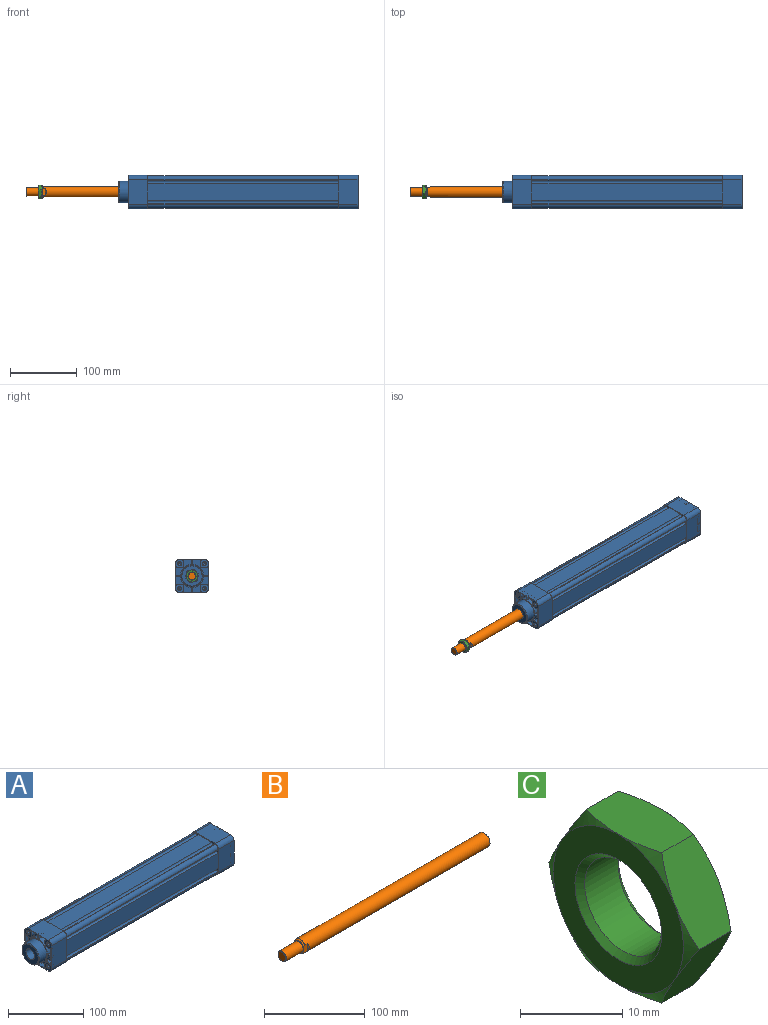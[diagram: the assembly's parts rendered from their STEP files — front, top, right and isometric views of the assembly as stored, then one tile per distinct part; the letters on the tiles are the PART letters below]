
ASSEMBLY  parts=3 mates=2
PART A: 303 faces, bbox 358x50x50 mm
  f0: plane 30.08x30.08mm, normal (-1,0,0), area 509.6mm2, adj f46,f302
  f1: plane 37x29mm, normal (0,1,0), area 866.6mm2, adj f3,f37,f43,f44,f276,f293
  f2: plane 37x29mm, normal (0,1,0), area 866.6mm2, adj f4,f29,f35,f36,f273,f281
  f3: plane 50x50mm, normal (1,0,0), area 1558.8mm2, adj f1,f37,f38,f39,f40,f41,f42,f43
  f4: plane 50x50mm, normal (-1,0,0), area 754.5mm2, adj f2,f29,f30,f31,f32,f33,f34,f35
  f5: cylinder r=2.5mm len=285mm, axis (-1,0,0), area 2238.4mm2, adj f6,f28,f36,f44
  f6: plane 285x1mm, normal (0,1,0), area 285mm2, adj f5,f7,f36,f44
  f7: cylinder r=5.5mm len=285mm, axis (-1,0,0), area 2462.2mm2, adj f6,f8,f36,f44
  f8: plane 285x1mm, normal (0,0,1), area 285mm2, adj f7,f9,f36,f44
  f9: cylinder r=2.5mm len=285mm, axis (-1,0,0), area 2238.4mm2, adj f8,f10,f36,f44
  f10: plane 285x25mm, normal (0,0,1), area 7125mm2, adj f9,f11,f36,f44
  f11: cylinder r=2.5mm len=285mm, axis (-1,0,0), area 2238.4mm2, adj f10,f12,f36,f44
  f12: plane 285x1mm, normal (0,0,1), area 285mm2, adj f11,f13,f36,f44
  f13: cylinder r=5.5mm len=285mm, axis (-1,0,0), area 2462.2mm2, adj f12,f14,f36,f44
  f14: plane 285x1mm, normal (0,-1,0), area 285mm2, adj f13,f15,f36,f44
  f15: cylinder r=2.5mm len=285mm, axis (-1,0,0), area 2238.4mm2, adj f14,f16,f36,f44
  f16: plane 285x25mm, normal (0,-1,0), area 7125mm2, adj f15,f17,f36,f44
  f17: cylinder r=2.5mm len=285mm, axis (-1,0,0), area 2238.4mm2, adj f16,f18,f36,f44
  f18: plane 285x1mm, normal (0,-1,0), area 285mm2, adj f17,f19,f36,f44
  f19: cylinder r=5.5mm len=285mm, axis (-1,0,0), area 2462.2mm2, adj f18,f20,f36,f44
  f20: plane 285x1mm, normal (0,0,-1), area 285mm2, adj f19,f21,f36,f44
  f21: cylinder r=2.5mm len=285mm, axis (-1,0,0), area 2238.4mm2, adj f20,f22,f36,f44
  f22: plane 285x25mm, normal (0,0,-1), area 7125mm2, adj f21,f23,f36,f44
  f23: cylinder r=2.5mm len=285mm, axis (-1,0,0), area 2238.4mm2, adj f22,f24,f36,f44
  f24: plane 285x1mm, normal (0,0,-1), area 285mm2, adj f23,f25,f36,f44
  f25: cylinder r=5.5mm len=285mm, axis (-1,0,0), area 2462.2mm2, adj f24,f26,f36,f44
  f26: plane 285x1mm, normal (0,1,0), area 285mm2, adj f25,f27,f36,f44
  f27: cylinder r=2.5mm len=285mm, axis (-1,0,0), area 2238.4mm2, adj f26,f28,f36,f44
  f28: plane 285x25mm, normal (0,1,0), area 7125mm2, adj f5,f27,f36,f44
  f29: cylinder r=6.5mm len=29mm, axis (-1,0,0), area 296.1mm2, adj f2,f4,f30,f36
  f30: plane 37x29mm, normal (0,0,1), area 1073mm2, adj f4,f29,f31,f36
  f31: cylinder r=6.5mm len=29mm, axis (-1,0,0), area 296.1mm2, adj f4,f30,f32,f36
  f32: plane 37x29mm, normal (0,-1,0), area 1073mm2, adj f4,f31,f33,f36
  f33: cylinder r=6.5mm len=29mm, axis (-1,0,0), area 296.1mm2, adj f4,f32,f34,f36
  f34: plane 37x29mm, normal (0,0,-1), area 1073mm2, adj f4,f33,f35,f36
  f35: cylinder r=6.5mm len=29mm, axis (-1,0,0), area 296.1mm2, adj f2,f4,f34,f36
  f36: plane 50x50mm, normal (1,0,0), area 264.2mm2, adj f2,f5,f6,f7,f8,f9,f10,f11
  f37: cylinder r=6.5mm len=29mm, axis (1,0,0), area 296.1mm2, adj f1,f3,f38,f44
  f38: plane 37x29mm, normal (0,0,-1), area 1073mm2, adj f3,f37,f39,f44
  f39: cylinder r=6.5mm len=29mm, axis (1,0,0), area 296.1mm2, adj f3,f38,f40,f44
  f40: plane 37x29mm, normal (0,-1,0), area 1073mm2, adj f3,f39,f41,f44
  f41: cylinder r=6.5mm len=29mm, axis (1,0,0), area 296.1mm2, adj f3,f40,f42,f44
  f42: plane 37x29mm, normal (0,0,1), area 1073mm2, adj f3,f41,f43,f44
  f43: cylinder r=6.5mm len=29mm, axis (1,0,0), area 296.1mm2, adj f1,f3,f42,f44
  f44: plane 50x50mm, normal (-1,0,0), area 264.2mm2, adj f1,f5,f6,f7,f8,f9,f10,f11
  f45: cylinder r=16mm len=32mm, axis (1,0,0), area 1411.5mm2, adj f4,f46
  f46: torus R=15.04mm, axis (1,0,0), area 148.3mm2, adj f0,f45
  f47: cylinder r=0.54mm len=6.42mm, axis (-1,0,0), area 5.4mm2, adj f4,f48,f56,f57
  f48: plane 12.46x6.42mm, normal (0,-1,0), area 80mm2, adj f4,f47,f49,f57
  f49: cylinder r=0.54mm len=6.42mm, axis (-1,0,0), area 8.2mm2, adj f4,f48,f50,f57
  f50: cylinder r=6.5mm len=8.45mm, axis (-1,0,0), area 59.2mm2, adj f4,f49,f51,f57
  f51: cylinder r=0.54mm len=6.42mm, axis (-1,0,0), area 4.9mm2, adj f4,f50,f52,f57
  f52: plane 6.42x0.89mm, normal (0,0.71,-0.71), area 8.1mm2, adj f4,f51,f53,f57
  f53: cylinder r=0.36mm len=6.42mm, axis (-1,0,0), area 3.5mm2, adj f4,f52,f54,f57
  f54: cylinder r=17.6mm len=10.99mm, axis (-1,0,0), area 77.9mm2, adj f4,f53,f55,f57
  f55: cylinder r=0.36mm len=6.42mm, axis (-1,0,0), area 3.5mm2, adj f4,f54,f56,f57
  f56: plane 6.42x5.52mm, normal (0,0,1), area 35.5mm2, adj f4,f47,f55,f57
  f57: plane 13.54x11.07mm, normal (-1,0,0), area 99mm2, adj f47,f48,f49,f50,f51,f52,f53,f54
  f58: cylinder r=0.54mm len=6.42mm, axis (-1,0,0), area 5.4mm2, adj f4,f59,f67,f68
  f59: plane 12.46x6.42mm, normal (0,0,-1), area 80mm2, adj f4,f58,f60,f68
  f60: cylinder r=0.54mm len=6.42mm, axis (-1,0,0), area 8.2mm2, adj f4,f59,f61,f68
  f61: cylinder r=6.5mm len=8.45mm, axis (-1,0,0), area 59.2mm2, adj f4,f60,f62,f68
  f62: cylinder r=0.54mm len=6.42mm, axis (-1,0,0), area 4.9mm2, adj f4,f61,f63,f68
  f63: plane 6.42x0.89mm, normal (0,0.71,0.71), area 8.1mm2, adj f4,f62,f64,f68
  f64: cylinder r=0.36mm len=6.42mm, axis (-1,0,0), area 3.5mm2, adj f4,f63,f65,f68
  f65: cylinder r=17.6mm len=10.99mm, axis (-1,0,0), area 77.9mm2, adj f4,f64,f66,f68
  f66: cylinder r=0.36mm len=6.42mm, axis (-1,0,0), area 3.5mm2, adj f4,f65,f67,f68
  f67: plane 6.42x5.52mm, normal (0,-1,0), area 35.5mm2, adj f4,f58,f66,f68
  f68: plane 13.54x11.07mm, normal (-1,0,0), area 99mm2, adj f58,f59,f60,f61,f62,f63,f64,f65
  f69: cylinder r=0.54mm len=6.42mm, axis (-1,0,0), area 5.4mm2, adj f4,f70,f78,f79
  f70: plane 12.46x6.42mm, normal (0,1,0), area 80mm2, adj f4,f69,f71,f79
  f71: cylinder r=0.54mm len=6.42mm, axis (-1,0,0), area 8.2mm2, adj f4,f70,f72,f79
  f72: cylinder r=6.5mm len=8.45mm, axis (-1,0,0), area 59.2mm2, adj f4,f71,f73,f79
  f73: cylinder r=0.54mm len=6.42mm, axis (-1,0,0), area 4.9mm2, adj f4,f72,f74,f79
  f74: plane 6.42x0.89mm, normal (0,-0.71,0.71), area 8.1mm2, adj f4,f73,f75,f79
  f75: cylinder r=0.36mm len=6.42mm, axis (-1,0,0), area 3.5mm2, adj f4,f74,f76,f79
  f76: cylinder r=17.6mm len=10.99mm, axis (-1,0,0), area 77.9mm2, adj f4,f75,f77,f79
  f77: cylinder r=0.36mm len=6.42mm, axis (-1,0,0), area 3.5mm2, adj f4,f76,f78,f79
  f78: plane 6.42x5.52mm, normal (0,0,-1), area 35.5mm2, adj f4,f69,f77,f79
  f79: plane 13.54x11.07mm, normal (-1,0,0), area 99mm2, adj f69,f70,f71,f72,f73,f74,f75,f76
  f80: cylinder r=0.54mm len=6.42mm, axis (-1,0,0), area 5.4mm2, adj f4,f81,f89,f90
  f81: plane 12.46x6.42mm, normal (0,0,1), area 80mm2, adj f4,f80,f82,f90
  f82: cylinder r=0.54mm len=6.42mm, axis (-1,0,0), area 8.2mm2, adj f4,f81,f83,f90
  f83: cylinder r=6.5mm len=8.45mm, axis (-1,0,0), area 59.2mm2, adj f4,f82,f84,f90
  f84: cylinder r=0.54mm len=6.42mm, axis (-1,0,0), area 4.9mm2, adj f4,f83,f85,f90
  f85: plane 6.42x0.89mm, normal (0,-0.71,-0.71), area 8.1mm2, adj f4,f84,f86,f90
  f86: cylinder r=0.36mm len=6.42mm, axis (-1,0,0), area 3.5mm2, adj f4,f85,f87,f90
  f87: cylinder r=17.6mm len=10.99mm, axis (-1,0,0), area 77.9mm2, adj f4,f86,f88,f90
  f88: cylinder r=0.36mm len=6.42mm, axis (-1,0,0), area 3.5mm2, adj f4,f87,f89,f90
  f89: plane 6.42x5.52mm, normal (0,1,0), area 35.5mm2, adj f4,f80,f88,f90
  f90: plane 13.54x11.07mm, normal (-1,0,0), area 99mm2, adj f80,f81,f82,f83,f84,f85,f86,f87
  f91: cylinder r=0.54mm len=6.42mm, axis (1,0,0), area 5.4mm2, adj f4,f92,f100,f101
  f92: plane 12.46x6.42mm, normal (0,-1,0), area 80mm2, adj f4,f91,f93,f101
  f93: cylinder r=0.54mm len=6.42mm, axis (1,0,0), area 8.2mm2, adj f4,f92,f94,f101
  f94: cylinder r=6.5mm len=8.45mm, axis (1,0,0), area 59.2mm2, adj f4,f93,f95,f101
  f95: cylinder r=0.54mm len=6.42mm, axis (1,0,0), area 4.9mm2, adj f4,f94,f96,f101
  f96: plane 6.42x0.89mm, normal (0,0.71,0.71), area 8.1mm2, adj f4,f95,f97,f101
  f97: cylinder r=0.36mm len=6.42mm, axis (1,0,0), area 3.5mm2, adj f4,f96,f98,f101
  f98: cylinder r=17.6mm len=10.99mm, axis (1,0,0), area 77.9mm2, adj f4,f97,f99,f101
  f99: cylinder r=0.36mm len=6.42mm, axis (1,0,0), area 3.5mm2, adj f4,f98,f100,f101
  f100: plane 6.42x5.52mm, normal (0,0,-1), area 35.5mm2, adj f4,f91,f99,f101
  f101: plane 13.54x11.07mm, normal (-1,0,0), area 99mm2, adj f91,f92,f93,f94,f95,f96,f97,f98
  f102: cylinder r=0.54mm len=6.42mm, axis (1,0,0), area 5.4mm2, adj f4,f103,f111,f112
  f103: plane 12.46x6.42mm, normal (0,0,-1), area 80mm2, adj f4,f102,f104,f112
  f104: cylinder r=0.54mm len=6.42mm, axis (1,0,0), area 8.2mm2, adj f4,f103,f105,f112
  f105: cylinder r=6.5mm len=8.45mm, axis (1,0,0), area 59.2mm2, adj f4,f104,f106,f112
  f106: cylinder r=0.54mm len=6.42mm, axis (1,0,0), area 4.9mm2, adj f4,f105,f107,f112
  f107: plane 6.42x0.89mm, normal (0,-0.71,0.71), area 8.1mm2, adj f4,f106,f108,f112
  f108: cylinder r=0.36mm len=6.42mm, axis (1,0,0), area 3.5mm2, adj f4,f107,f109,f112
  f109: cylinder r=17.6mm len=10.99mm, axis (1,0,0), area 77.9mm2, adj f4,f108,f110,f112
  f110: cylinder r=0.36mm len=6.42mm, axis (1,0,0), area 3.5mm2, adj f4,f109,f111,f112
  f111: plane 6.42x5.52mm, normal (0,1,0), area 35.5mm2, adj f4,f102,f110,f112
  f112: plane 13.54x11.07mm, normal (-1,0,0), area 99mm2, adj f102,f103,f104,f105,f106,f107,f108,f109
  f113: cylinder r=0.54mm len=6.42mm, axis (1,0,0), area 5.4mm2, adj f4,f114,f122,f123
  f114: plane 12.46x6.42mm, normal (0,1,0), area 80mm2, adj f4,f113,f115,f123
  f115: cylinder r=0.54mm len=6.42mm, axis (1,0,0), area 8.2mm2, adj f4,f114,f116,f123
  f116: cylinder r=6.5mm len=8.45mm, axis (1,0,0), area 59.2mm2, adj f4,f115,f117,f123
  f117: cylinder r=0.54mm len=6.42mm, axis (1,0,0), area 4.9mm2, adj f4,f116,f118,f123
  f118: plane 6.42x0.89mm, normal (0,-0.71,-0.71), area 8.1mm2, adj f4,f117,f119,f123
  f119: cylinder r=0.36mm len=6.42mm, axis (1,0,0), area 3.5mm2, adj f4,f118,f120,f123
  f120: cylinder r=17.6mm len=10.99mm, axis (1,0,0), area 77.9mm2, adj f4,f119,f121,f123
  f121: cylinder r=0.36mm len=6.42mm, axis (1,0,0), area 3.5mm2, adj f4,f120,f122,f123
  f122: plane 6.42x5.52mm, normal (0,0,1), area 35.5mm2, adj f4,f113,f121,f123
  f123: plane 13.54x11.07mm, normal (-1,0,0), area 99mm2, adj f113,f114,f115,f116,f117,f118,f119,f120
  f124: cylinder r=0.54mm len=6.42mm, axis (1,0,0), area 5.4mm2, adj f4,f125,f133,f134
  f125: plane 12.46x6.42mm, normal (0,0,1), area 80mm2, adj f4,f124,f126,f134
  f126: cylinder r=0.54mm len=6.42mm, axis (1,0,0), area 8.2mm2, adj f4,f125,f127,f134
  f127: cylinder r=6.5mm len=8.45mm, axis (1,0,0), area 59.2mm2, adj f4,f126,f128,f134
  f128: cylinder r=0.54mm len=6.42mm, axis (1,0,0), area 4.9mm2, adj f4,f127,f129,f134
  f129: plane 6.42x0.89mm, normal (0,0.71,-0.71), area 8.1mm2, adj f4,f128,f130,f134
  f130: cylinder r=0.36mm len=6.42mm, axis (1,0,0), area 3.5mm2, adj f4,f129,f131,f134
  f131: cylinder r=17.6mm len=10.99mm, axis (1,0,0), area 77.9mm2, adj f4,f130,f132,f134
  f132: cylinder r=0.36mm len=6.42mm, axis (1,0,0), area 3.5mm2, adj f4,f131,f133,f134
  f133: plane 6.42x5.52mm, normal (0,-1,0), area 35.5mm2, adj f4,f124,f132,f134
  f134: plane 13.54x11.07mm, normal (-1,0,0), area 99mm2, adj f124,f125,f126,f127,f128,f129,f130,f131
  f135: cylinder r=0.54mm len=6.42mm, axis (1,0,0), area 5.4mm2, adj f3,f136,f144,f145
  f136: plane 12.46x6.42mm, normal (0,-1,0), area 80mm2, adj f3,f135,f137,f145
  f137: cylinder r=0.54mm len=6.42mm, axis (1,0,0), area 8.2mm2, adj f3,f136,f138,f145
  f138: cylinder r=6.5mm len=8.45mm, axis (1,0,0), area 59.2mm2, adj f3,f137,f139,f145
  f139: cylinder r=0.54mm len=6.42mm, axis (1,0,0), area 4.9mm2, adj f3,f138,f140,f145
  f140: plane 6.42x0.89mm, normal (0,0.71,0.71), area 8.1mm2, adj f3,f139,f141,f145
  f141: cylinder r=0.36mm len=6.42mm, axis (1,0,0), area 3.5mm2, adj f3,f140,f142,f145
  f142: cylinder r=17.6mm len=10.99mm, axis (1,0,0), area 77.9mm2, adj f3,f141,f143,f145
  f143: cylinder r=0.36mm len=6.42mm, axis (1,0,0), area 3.5mm2, adj f3,f142,f144,f145
  f144: plane 6.42x5.52mm, normal (0,0,-1), area 35.5mm2, adj f3,f135,f143,f145
  f145: plane 13.54x11.07mm, normal (1,0,0), area 99mm2, adj f135,f136,f137,f138,f139,f140,f141,f142
  f146: cylinder r=0.54mm len=6.42mm, axis (1,0,0), area 5.4mm2, adj f3,f147,f155,f156
  f147: plane 12.46x6.42mm, normal (0,0,-1), area 80mm2, adj f3,f146,f148,f156
  f148: cylinder r=0.54mm len=6.42mm, axis (1,0,0), area 8.2mm2, adj f3,f147,f149,f156
  f149: cylinder r=6.5mm len=8.45mm, axis (1,0,0), area 59.2mm2, adj f3,f148,f150,f156
  f150: cylinder r=0.54mm len=6.42mm, axis (1,0,0), area 4.9mm2, adj f3,f149,f151,f156
  f151: plane 6.42x0.89mm, normal (0,-0.71,0.71), area 8.1mm2, adj f3,f150,f152,f156
  f152: cylinder r=0.36mm len=6.42mm, axis (1,0,0), area 3.5mm2, adj f3,f151,f153,f156
  f153: cylinder r=17.6mm len=10.99mm, axis (1,0,0), area 77.9mm2, adj f3,f152,f154,f156
  f154: cylinder r=0.36mm len=6.42mm, axis (1,0,0), area 3.5mm2, adj f3,f153,f155,f156
  f155: plane 6.42x5.52mm, normal (0,1,0), area 35.5mm2, adj f3,f146,f154,f156
  f156: plane 13.54x11.07mm, normal (1,0,0), area 99mm2, adj f146,f147,f148,f149,f150,f151,f152,f153
  f157: cylinder r=0.54mm len=6.42mm, axis (1,0,0), area 5.4mm2, adj f3,f158,f166,f167
  f158: plane 12.46x6.42mm, normal (0,1,0), area 80mm2, adj f3,f157,f159,f167
  f159: cylinder r=0.54mm len=6.42mm, axis (1,0,0), area 8.2mm2, adj f3,f158,f160,f167
  f160: cylinder r=6.5mm len=8.45mm, axis (1,0,0), area 59.2mm2, adj f3,f159,f161,f167
  f161: cylinder r=0.54mm len=6.42mm, axis (1,0,0), area 4.9mm2, adj f3,f160,f162,f167
  f162: plane 6.42x0.89mm, normal (0,-0.71,-0.71), area 8.1mm2, adj f3,f161,f163,f167
  f163: cylinder r=0.36mm len=6.42mm, axis (1,0,0), area 3.5mm2, adj f3,f162,f164,f167
  f164: cylinder r=17.6mm len=10.99mm, axis (1,0,0), area 77.9mm2, adj f3,f163,f165,f167
  f165: cylinder r=0.36mm len=6.42mm, axis (1,0,0), area 3.5mm2, adj f3,f164,f166,f167
  f166: plane 6.42x5.52mm, normal (0,0,1), area 35.5mm2, adj f3,f157,f165,f167
  f167: plane 13.54x11.07mm, normal (1,0,0), area 99mm2, adj f157,f158,f159,f160,f161,f162,f163,f164
  f168: cylinder r=0.54mm len=6.42mm, axis (1,0,0), area 5.4mm2, adj f3,f169,f177,f178
  f169: plane 12.46x6.42mm, normal (0,0,1), area 80mm2, adj f3,f168,f170,f178
  f170: cylinder r=0.54mm len=6.42mm, axis (1,0,0), area 8.2mm2, adj f3,f169,f171,f178
  f171: cylinder r=6.5mm len=8.45mm, axis (1,0,0), area 59.2mm2, adj f3,f170,f172,f178
  f172: cylinder r=0.54mm len=6.42mm, axis (1,0,0), area 4.9mm2, adj f3,f171,f173,f178
  f173: plane 6.42x0.89mm, normal (0,0.71,-0.71), area 8.1mm2, adj f3,f172,f174,f178
  f174: cylinder r=0.36mm len=6.42mm, axis (1,0,0), area 3.5mm2, adj f3,f173,f175,f178
  f175: cylinder r=17.6mm len=10.99mm, axis (1,0,0), area 77.9mm2, adj f3,f174,f176,f178
  f176: cylinder r=0.36mm len=6.42mm, axis (1,0,0), area 3.5mm2, adj f3,f175,f177,f178
  f177: plane 6.42x5.52mm, normal (0,-1,0), area 35.5mm2, adj f3,f168,f176,f178
  f178: plane 13.54x11.07mm, normal (1,0,0), area 99mm2, adj f168,f169,f170,f171,f172,f173,f174,f175
  f179: cylinder r=0.54mm len=6.42mm, axis (-1,0,0), area 5.4mm2, adj f3,f180,f188,f189
  f180: plane 12.46x6.42mm, normal (0,-1,0), area 80mm2, adj f3,f179,f181,f189
  f181: cylinder r=0.54mm len=6.42mm, axis (-1,0,0), area 8.2mm2, adj f3,f180,f182,f189
  f182: cylinder r=6.5mm len=8.45mm, axis (-1,0,0), area 59.2mm2, adj f3,f181,f183,f189
  f183: cylinder r=0.54mm len=6.42mm, axis (-1,0,0), area 4.9mm2, adj f3,f182,f184,f189
  f184: plane 6.42x0.89mm, normal (0,0.71,-0.71), area 8.1mm2, adj f3,f183,f185,f189
  f185: cylinder r=0.36mm len=6.42mm, axis (-1,0,0), area 3.5mm2, adj f3,f184,f186,f189
  f186: cylinder r=17.6mm len=10.99mm, axis (-1,0,0), area 77.9mm2, adj f3,f185,f187,f189
  f187: cylinder r=0.36mm len=6.42mm, axis (-1,0,0), area 3.5mm2, adj f3,f186,f188,f189
  f188: plane 6.42x5.52mm, normal (0,0,1), area 35.5mm2, adj f3,f179,f187,f189
  f189: plane 13.54x11.07mm, normal (1,0,0), area 99mm2, adj f179,f180,f181,f182,f183,f184,f185,f186
  f190: cylinder r=0.54mm len=6.42mm, axis (-1,0,0), area 5.4mm2, adj f3,f191,f199,f200
  f191: plane 12.46x6.42mm, normal (0,0,-1), area 80mm2, adj f3,f190,f192,f200
  f192: cylinder r=0.54mm len=6.42mm, axis (-1,0,0), area 8.2mm2, adj f3,f191,f193,f200
  f193: cylinder r=6.5mm len=8.45mm, axis (-1,0,0), area 59.2mm2, adj f3,f192,f194,f200
  f194: cylinder r=0.54mm len=6.42mm, axis (-1,0,0), area 4.9mm2, adj f3,f193,f195,f200
  f195: plane 6.42x0.89mm, normal (0,0.71,0.71), area 8.1mm2, adj f3,f194,f196,f200
  f196: cylinder r=0.36mm len=6.42mm, axis (-1,0,0), area 3.5mm2, adj f3,f195,f197,f200
  f197: cylinder r=17.6mm len=10.99mm, axis (-1,0,0), area 77.9mm2, adj f3,f196,f198,f200
  f198: cylinder r=0.36mm len=6.42mm, axis (-1,0,0), area 3.5mm2, adj f3,f197,f199,f200
  f199: plane 6.42x5.52mm, normal (0,-1,0), area 35.5mm2, adj f3,f190,f198,f200
  f200: plane 13.54x11.07mm, normal (1,0,0), area 99mm2, adj f190,f191,f192,f193,f194,f195,f196,f197
  f201: cylinder r=0.54mm len=6.42mm, axis (-1,0,0), area 5.4mm2, adj f3,f202,f210,f211
  f202: plane 12.46x6.42mm, normal (0,1,0), area 80mm2, adj f3,f201,f203,f211
  f203: cylinder r=0.54mm len=6.42mm, axis (-1,0,0), area 8.2mm2, adj f3,f202,f204,f211
  f204: cylinder r=6.5mm len=8.45mm, axis (-1,0,0), area 59.2mm2, adj f3,f203,f205,f211
  f205: cylinder r=0.54mm len=6.42mm, axis (-1,0,0), area 4.9mm2, adj f3,f204,f206,f211
  f206: plane 6.42x0.89mm, normal (0,-0.71,0.71), area 8.1mm2, adj f3,f205,f207,f211
  f207: cylinder r=0.36mm len=6.42mm, axis (-1,0,0), area 3.5mm2, adj f3,f206,f208,f211
  f208: cylinder r=17.6mm len=10.99mm, axis (-1,0,0), area 77.9mm2, adj f3,f207,f209,f211
  f209: cylinder r=0.36mm len=6.42mm, axis (-1,0,0), area 3.5mm2, adj f3,f208,f210,f211
  f210: plane 6.42x5.52mm, normal (0,0,-1), area 35.5mm2, adj f3,f201,f209,f211
  f211: plane 13.54x11.07mm, normal (1,0,0), area 99mm2, adj f201,f202,f203,f204,f205,f206,f207,f208
  f212: cylinder r=0.54mm len=6.42mm, axis (-1,0,0), area 5.4mm2, adj f3,f213,f221,f222
  f213: plane 12.46x6.42mm, normal (0,0,1), area 80mm2, adj f3,f212,f214,f222
  f214: cylinder r=0.54mm len=6.42mm, axis (-1,0,0), area 8.2mm2, adj f3,f213,f215,f222
  f215: cylinder r=6.5mm len=8.45mm, axis (-1,0,0), area 59.2mm2, adj f3,f214,f216,f222
  f216: cylinder r=0.54mm len=6.42mm, axis (-1,0,0), area 4.9mm2, adj f3,f215,f217,f222
  f217: plane 6.42x0.89mm, normal (0,-0.71,-0.71), area 8.1mm2, adj f3,f216,f218,f222
  f218: cylinder r=0.36mm len=6.42mm, axis (-1,0,0), area 3.5mm2, adj f3,f217,f219,f222
  f219: cylinder r=17.6mm len=10.99mm, axis (-1,0,0), area 77.9mm2, adj f3,f218,f220,f222
  f220: cylinder r=0.36mm len=6.42mm, axis (-1,0,0), area 3.5mm2, adj f3,f219,f221,f222
  f221: plane 6.42x5.52mm, normal (0,1,0), area 35.5mm2, adj f3,f212,f220,f222
  f222: plane 13.54x11.07mm, normal (1,0,0), area 99mm2, adj f212,f213,f214,f215,f216,f217,f218,f219
  f223: cone r=0mm half-angle=60deg, axis (-1,0,0), area 21.9mm2, adj f224
  f224: cylinder r=2.46mm len=4.92mm, axis (-1,0,0), area 38mm2, adj f223,f225
  f225: cone r=2.46mm half-angle=45deg, axis (-1,0,0), area 13.1mm2, adj f224,f226
  f226: plane 6x6mm, normal (1,0,0), area 9.3mm2, adj f225,f227
  f227: cylinder r=2.46mm len=11.46mm, axis (-1,0,0), area 177mm2, adj f226,f228
  f228: cone r=2.46mm half-angle=45deg, axis (-1,0,0), area 13.1mm2, adj f4,f227
  f229: cone r=0mm half-angle=60deg, axis (-1,0,0), area 21.9mm2, adj f230
  f230: cylinder r=2.46mm len=4.92mm, axis (-1,0,0), area 38mm2, adj f229,f231
  f231: cone r=2.46mm half-angle=45deg, axis (-1,0,0), area 13.1mm2, adj f230,f232
  f232: plane 6x6mm, normal (1,0,0), area 9.3mm2, adj f231,f233
  f233: cylinder r=2.46mm len=11.46mm, axis (-1,0,0), area 177mm2, adj f232,f234
  f234: cone r=2.46mm half-angle=45deg, axis (-1,0,0), area 13.1mm2, adj f4,f233
  f235: cone r=0mm half-angle=60deg, axis (-1,0,0), area 21.9mm2, adj f236
  f236: cylinder r=2.46mm len=4.92mm, axis (-1,0,0), area 38mm2, adj f235,f237
  f237: cone r=2.46mm half-angle=45deg, axis (-1,0,0), area 13.1mm2, adj f236,f238
  f238: plane 6x6mm, normal (1,0,0), area 9.3mm2, adj f237,f239
  f239: cylinder r=2.46mm len=11.46mm, axis (-1,0,0), area 177mm2, adj f238,f240
  f240: cone r=2.46mm half-angle=45deg, axis (-1,0,0), area 13.1mm2, adj f4,f239
  f241: cone r=0mm half-angle=60deg, axis (-1,0,0), area 21.9mm2, adj f242
  f242: cylinder r=2.46mm len=4.92mm, axis (-1,0,0), area 38mm2, adj f241,f243
  f243: cone r=2.46mm half-angle=45deg, axis (-1,0,0), area 13.1mm2, adj f242,f244
  f244: plane 6x6mm, normal (1,0,0), area 9.3mm2, adj f243,f245
  f245: cylinder r=2.46mm len=11.46mm, axis (-1,0,0), area 177mm2, adj f244,f246
  f246: cone r=2.46mm half-angle=45deg, axis (-1,0,0), area 13.1mm2, adj f4,f245
  f247: cone r=0mm half-angle=60deg, axis (1,0,0), area 21.9mm2, adj f248
  f248: cylinder r=2.46mm len=4.92mm, axis (1,0,0), area 38mm2, adj f247,f249
  f249: cone r=2.46mm half-angle=45deg, axis (1,0,0), area 13.1mm2, adj f248,f250
  f250: plane 6x6mm, normal (-1,0,0), area 9.3mm2, adj f249,f251
  f251: cylinder r=2.46mm len=11.46mm, axis (1,0,0), area 177mm2, adj f250,f252
  f252: cone r=2.46mm half-angle=45deg, axis (1,0,0), area 13.1mm2, adj f3,f251
  f253: cone r=0mm half-angle=60deg, axis (1,0,0), area 21.9mm2, adj f254
  f254: cylinder r=2.46mm len=4.92mm, axis (1,0,0), area 38mm2, adj f253,f255
  f255: cone r=2.46mm half-angle=45deg, axis (1,0,0), area 13.1mm2, adj f254,f256
  f256: plane 6x6mm, normal (-1,0,0), area 9.3mm2, adj f255,f257
  f257: cylinder r=2.46mm len=11.46mm, axis (1,0,0), area 177mm2, adj f256,f258
  f258: cone r=2.46mm half-angle=45deg, axis (1,0,0), area 13.1mm2, adj f3,f257
  f259: cone r=0mm half-angle=60deg, axis (1,0,0), area 21.9mm2, adj f260
  f260: cylinder r=2.46mm len=4.92mm, axis (1,0,0), area 38mm2, adj f259,f261
  f261: cone r=2.46mm half-angle=45deg, axis (1,0,0), area 13.1mm2, adj f260,f262
  f262: plane 6x6mm, normal (-1,0,0), area 9.3mm2, adj f261,f263
  f263: cylinder r=2.46mm len=11.46mm, axis (1,0,0), area 177mm2, adj f262,f264
  f264: cone r=2.46mm half-angle=45deg, axis (1,0,0), area 13.1mm2, adj f3,f263
  f265: cone r=0mm half-angle=60deg, axis (1,0,0), area 21.9mm2, adj f266
  f266: cylinder r=2.46mm len=4.92mm, axis (1,0,0), area 38mm2, adj f265,f267
  f267: cone r=2.46mm half-angle=45deg, axis (1,0,0), area 13.1mm2, adj f266,f268
  f268: plane 6x6mm, normal (-1,0,0), area 9.3mm2, adj f267,f269
  f269: cylinder r=2.46mm len=11.46mm, axis (1,0,0), area 177mm2, adj f268,f270
  f270: cone r=2.46mm half-angle=45deg, axis (1,0,0), area 13.1mm2, adj f3,f269
  f271: plane 11.45x11.45mm, normal (0,1,0), area 102.9mm2, adj f272
  f272: cylinder r=5.72mm len=12.3mm, axis (0,1,0), area 442.3mm2, adj f271,f273
  f273: cone r=5.72mm half-angle=45deg, axis (0,1,0), area 46.8mm2, adj f2,f272
  f274: plane 11.45x11.45mm, normal (0,1,0), area 102.9mm2, adj f275
  f275: cylinder r=5.72mm len=12.3mm, axis (0,1,0), area 442.3mm2, adj f274,f276
  f276: cone r=5.72mm half-angle=45deg, axis (0,1,0), area 46.8mm2, adj f1,f275
  f277: plane 8.61x8.61mm, normal (0,1,0), area 39.9mm2, adj f278,f282,f283,f284,f285,f286,f287
  f278: torus R=4.3mm, axis (0,-1,0), area 13.3mm2, adj f277,f279
  f279: cylinder r=4.6mm len=9.21mm, axis (0,-1,0), area 105.5mm2, adj f278,f280
  f280: plane 9.47x9.47mm, normal (0,1,0), area 3.9mm2, adj f279,f281
  f281: cylinder r=4.74mm len=9.47mm, axis (0,-1,0), area 206.7mm2, adj f2,f280
  f282: plane 4.61x2.3mm, normal (0.87,0,-0.5), area 12.2mm2, adj f277,f283,f287,f288
  f283: plane 4.61x2.3mm, normal (0.87,0,0.5), area 12.2mm2, adj f277,f282,f284,f288
  f284: plane 4.61x2.66mm, normal (0,0,1), area 12.2mm2, adj f277,f283,f285,f288
  f285: plane 4.61x2.3mm, normal (-0.87,0,0.5), area 12.2mm2, adj f277,f284,f286,f288
  f286: plane 4.61x2.3mm, normal (-0.87,0,-0.5), area 12.2mm2, adj f277,f285,f287,f288
  f287: plane 4.61x2.66mm, normal (0,0,-1), area 12.2mm2, adj f277,f282,f286,f288
  f288: plane 5.32x4.61mm, normal (0,1,0), area 18.4mm2, adj f282,f283,f284,f285,f286,f287
  f289: plane 8.61x8.61mm, normal (0,1,0), area 39.9mm2, adj f290,f294,f295,f296,f297,f298,f299
  f290: torus R=4.3mm, axis (0,-1,0), area 13.3mm2, adj f289,f291
  f291: cylinder r=4.6mm len=9.21mm, axis (0,-1,0), area 105.5mm2, adj f290,f292
  f292: plane 9.47x9.47mm, normal (0,1,0), area 3.9mm2, adj f291,f293
  f293: cylinder r=4.74mm len=9.47mm, axis (0,-1,0), area 206.7mm2, adj f1,f292
  f294: plane 4.61x2.3mm, normal (0.87,0,-0.5), area 12.2mm2, adj f289,f295,f299,f300
  f295: plane 4.61x2.3mm, normal (0.87,0,0.5), area 12.2mm2, adj f289,f294,f296,f300
  f296: plane 4.61x2.66mm, normal (0,0,1), area 12.2mm2, adj f289,f295,f297,f300
  f297: plane 4.61x2.3mm, normal (-0.87,0,0.5), area 12.2mm2, adj f289,f296,f298,f300
  f298: plane 4.61x2.3mm, normal (-0.87,0,-0.5), area 12.2mm2, adj f289,f297,f299,f300
  f299: plane 4.61x2.66mm, normal (0,0,-1), area 12.2mm2, adj f289,f294,f298,f300
  f300: plane 5.32x4.61mm, normal (0,1,0), area 18.4mm2, adj f294,f295,f296,f297,f298,f299
  f301: plane 16x16mm, normal (-1,0,0), area 201.1mm2, adj f302
  f302: cylinder r=8mm len=250mm, axis (-1,0,0), area 12566.4mm2, adj f0,f301
PART B: 12 faces, bbox 284x16x16 mm
  f0: cylinder r=8mm len=258.27mm, axis (-1,0,0), area 12897.1mm2, adj f1,f2,f4,f8,f9,f10,f11
  f1: cone r=8mm half-angle=30deg, axis (1,0,0), area 31.6mm2, adj f0,f3,f9,f11
  f2: cone r=8mm half-angle=30deg, axis (1,0,0), area 31.6mm2, adj f0,f3,f9,f11
  f3: plane 14x13mm, normal (-1,0,0), area 37.4mm2, adj f1,f2,f5,f9,f11
  f4: plane 16x16mm, normal (1,0,0), area 201.1mm2, adj f0
  f5: cylinder r=6mm len=23.32mm, axis (-1,0,0), area 879.3mm2, adj f3,f6
  f6: cone r=6mm half-angle=45deg, axis (1,0,0), area 34mm2, adj f5,f7
  f7: plane 10.65x10.65mm, normal (-1,0,0), area 89mm2, adj f6
  f8: plane 9.33x1.5mm, normal (-0.71,0.71,0), area 13.5mm2, adj f0,f9
  f9: plane 9.33x5mm, normal (0,1,0), area 43.3mm2, adj f0,f1,f2,f3,f8
  f10: plane 9.33x1.5mm, normal (-0.71,-0.71,0), area 13.5mm2, adj f0,f11
  f11: plane 9.33x5mm, normal (0,-1,0), area 43.3mm2, adj f0,f1,f2,f3,f10
PART C: 23 faces, bbox 6.9x21.6x21.6 mm
  f0: cone r=9mm half-angle=60deg, axis (1,0,0), area 8mm2, adj f13,f19,f20
  f1: cone r=9mm half-angle=60deg, axis (1,0,0), area 8mm2, adj f13,f18,f19
  f2: cone r=9mm half-angle=60deg, axis (1,0,0), area 8mm2, adj f13,f17,f18
  f3: cone r=9mm half-angle=60deg, axis (1,0,0), area 8mm2, adj f13,f20,f21
  f4: cone r=9mm half-angle=60deg, axis (1,0,0), area 8mm2, adj f13,f17,f22
  f5: cone r=9mm half-angle=60deg, axis (1,0,0), area 8mm2, adj f13,f21,f22
  f6: cone r=10.39mm half-angle=60deg, axis (-1,0,0), area 8mm2, adj f14,f17,f22
  f7: cone r=10.39mm half-angle=60deg, axis (-1,0,0), area 8mm2, adj f14,f17,f18
  f8: cone r=10.39mm half-angle=60deg, axis (-1,0,0), area 8mm2, adj f14,f18,f19
  f9: cone r=10.39mm half-angle=60deg, axis (-1,0,0), area 8mm2, adj f14,f19,f20
  f10: cone r=10.39mm half-angle=60deg, axis (-1,0,0), area 8mm2, adj f14,f20,f21
  f11: cone r=10.39mm half-angle=60deg, axis (-1,0,0), area 8mm2, adj f14,f21,f22
  f12: cone r=5.32mm half-angle=45deg, axis (-1,0,0), area 34mm2, adj f13,f16
  f13: plane 18x18mm, normal (-1,0,0), area 141.4mm2, adj f0,f1,f2,f3,f4,f5,f12
  f14: plane 18x18mm, normal (1,0,0), area 141.4mm2, adj f6,f7,f8,f9,f10,f11,f15
  f15: cone r=6mm half-angle=45deg, axis (1,0,0), area 34mm2, adj f14,f16
  f16: cylinder r=5.32mm len=10.65mm, axis (-1,0,0), area 155.4mm2, adj f12,f15
  f17: plane 9.85x6.87mm, normal (0,-0.87,0.5), area 56.6mm2, adj f2,f4,f6,f7,f18,f22
  f18: plane 9.85x6.87mm, normal (0,-0.87,-0.5), area 56.6mm2, adj f1,f2,f7,f8,f17,f19
  f19: plane 11.26x6.86mm, normal (0,0,-1), area 56.6mm2, adj f0,f1,f8,f9,f18,f20
  f20: plane 9.85x6.87mm, normal (0,0.87,-0.5), area 56.6mm2, adj f0,f3,f9,f10,f19,f21
  f21: plane 9.85x6.87mm, normal (0,0.87,0.5), area 56.6mm2, adj f3,f5,f10,f11,f20,f22
  f22: plane 11.26x6.86mm, normal (0,0,1), area 56.6mm2, adj f4,f5,f6,f11,f17,f21
PLACE A t=(21.75,31.55,68.21)mm fixed
PLACE B t=(-82.53,31.55,68.21)mm
PLACE C rot(axis=(-1,0,0),17.6deg) t=(-73.53,31.55,68.21)mm
MATE slider A.f45 <-> B.f0  axis (-1,0,0) through (21.75,31.55,68.21)mm
MATE cylindrical B.f0 <-> C.f0  axis (-1,0,0) through (-116.53,31.55,68.21)mm
